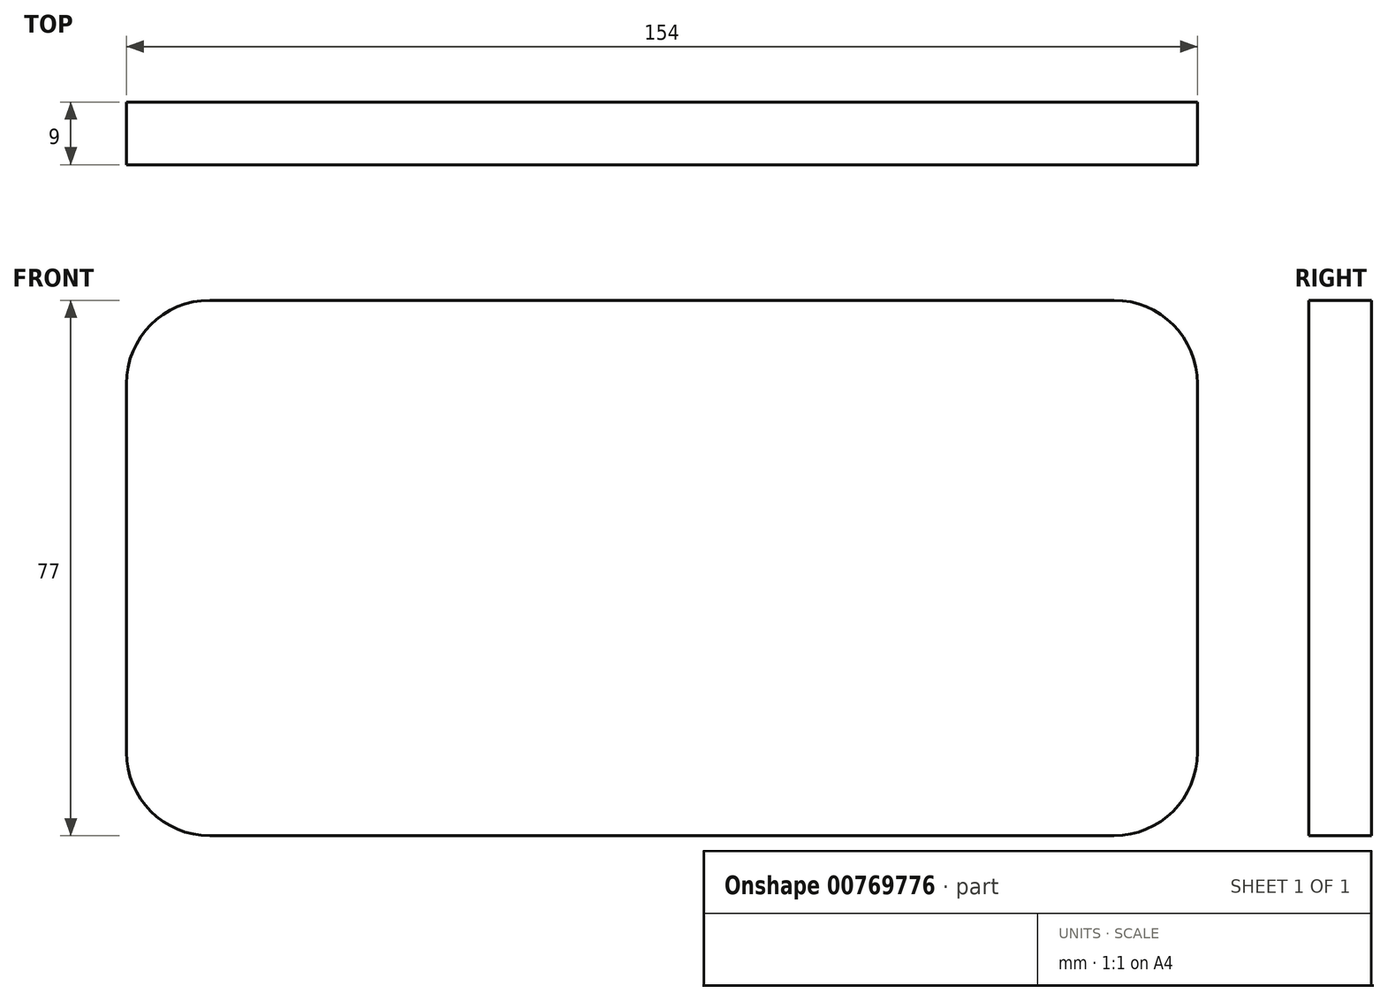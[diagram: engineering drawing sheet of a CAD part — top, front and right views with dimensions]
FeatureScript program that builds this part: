
annotation { "Feature Type Name" : "Feature", "Feature Type Description" : "" }
export const myFeature = defineFeature(function(context is Context, id is Id, definition is map)
    precondition{}
    {
        {
            var Q0;
            Q0=qCreatedBy(makeId("Front.planeOp"),FACE);
            var sketch = newSketch(context, id + "F0", { "sketchPlane" : qUnion([Q0])});
            skLineSegment(sketch, "E0.bottom", {"start": v(77, 38.5) * mm, "end": v(-77, 38.5) * mm});
            skLineSegment(sketch, "E0.top", {"start": v(77, -38.5) * mm, "end": v(-77, -38.5) * mm});
            skLineSegment(sketch, "E0.left", {"start": v(77, 38.5) * mm, "end": v(77, -38.5) * mm});
            skLineSegment(sketch, "E0.right", {"start": v(-77, 38.5) * mm, "end": v(-77, -38.5) * mm});
            skPoint(sketch, "E0.middle", {"position": v(0, 0) * mm});
            skSolve(sketch);
        }
        {
            var Q0;
            Q0 = qSketchRegion(id + "F0", true);
            extrude(context, id + "F1", {"entities" : qUnion([Q0]), "depth" : 9 * mm, "offsetDistance" : 25 * mm});
        }
        {
            var Q0;
            Q0=makeQuery(id+"F1.opExtrude","SWEPT_EDGE",EDGE,{"disambiguationData":[OSD([sQuery(id+"F0.wireOp",EDGE,"E0.top"),sQuery(id+"F0.wireOp",EDGE,"E0.left")])]});
            var Q1;
            Q1=makeQuery(id+"F1.opExtrude","SWEPT_EDGE",EDGE,{"disambiguationData":[OSD([sQuery(id+"F0.wireOp",EDGE,"E0.bottom"),sQuery(id+"F0.wireOp",EDGE,"E0.left")])]});
            var Q2;
            Q2=makeQuery(id+"F1.opExtrude","SWEPT_EDGE",EDGE,{"disambiguationData":[OSD([sQuery(id+"F0.wireOp",EDGE,"E0.top"),sQuery(id+"F0.wireOp",EDGE,"E0.right")])]});
            var Q3;
            Q3=makeQuery(id+"F1.opExtrude","SWEPT_EDGE",EDGE,{"disambiguationData":[OSD([sQuery(id+"F0.wireOp",EDGE,"E0.bottom"),sQuery(id+"F0.wireOp",EDGE,"E0.right")])]});
            fillet(context, id + "F2", {"entities" : qUnion([Q0, Q1, Q2, Q3]), "tangentPropagation" : true, "radius" : 12 * mm, "defaultsChanged" : true, "vertexSettings" : [], "allowEdgeOverflow" : false});
        }
    });
